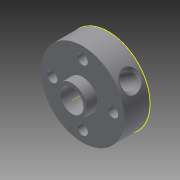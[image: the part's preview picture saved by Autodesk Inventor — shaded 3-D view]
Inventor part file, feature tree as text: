
AUTODESK INVENTOR PART (.ipt)
format: ipt  version: 2015 (Build 190159000, 159)  size: 187,904 bytes
history: native  units: in
note: dims shown in document units (in); Inventor stores cm internally (conversion verified against a paired STEP export)
features: other x14, sketch x1, imported_body x1, projected_geometry x1
ambient origin geometry x8: Origin, YZ Plane, XZ Plane, XY Plane, X Axis, Y Axis, Z Axis, Center Point
bodies: Body1 (feature_tree)
feature tree (17):
  other  "hub_motor_shaft_2012"
  other  "hub_motor_shaft_20121"
  other  "A_1"
  other  "A_2"
  other  "A_3"
  other  "A_4"
  other  "A_5"
  other  "A_6"
  other  "A_7"
  other  "A_8"
  other  "FRONT"
  other  "TOP"
  other  "RIGHT"
  other  "DTM1"
  sketch  "Sketch1"
  imported_body  "Base1"
  projected_geometry  "Projected Loop1"
